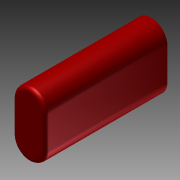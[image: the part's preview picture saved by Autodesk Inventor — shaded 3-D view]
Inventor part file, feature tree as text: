
AUTODESK INVENTOR PART (.ipt)
format: ipt  version: 2011 (Build 150239000, 239)  size: 87,040 bytes
history: native  units: mm (DEFAULTED — no unit token found)
features: extrude x1, fillet x1, sketch x1, reference x1
ambient origin geometry x8: Origin, YZ Plane, XZ Plane, XY Plane, X Axis, Y Axis, Z Axis, Center Point
bodies: Solid1 (feature_tree)
feature tree (4):
  extrude  "Extrusion1"  Depth=0.381mm
  fillet  "Fillet1"  [1 undecoded]
  sketch  "Sketch1"  dims[d0=12.7mm d1=0.0mm d2=0.381mm]
  reference  "Reference1"
note: 1 required parameter value undecoded (feature->parameter linkage not recoverable at this tier; creation-order binding heuristic only, values carry confidence <= 0.55)
